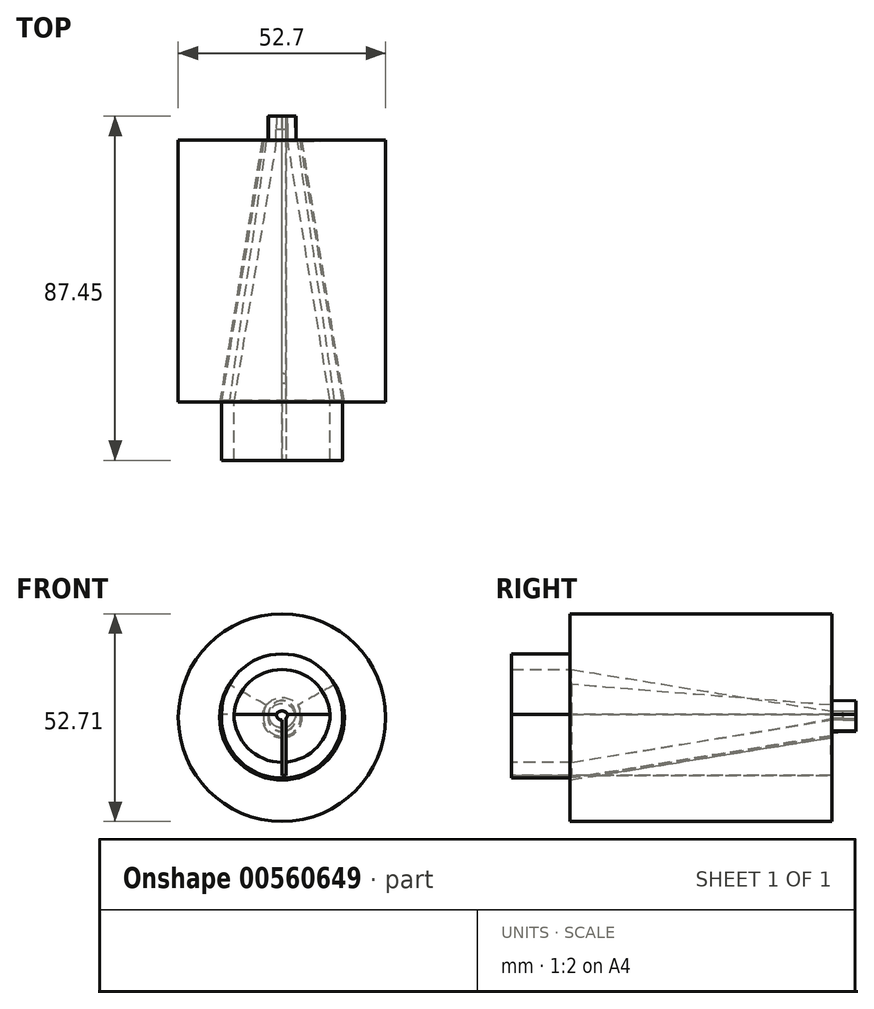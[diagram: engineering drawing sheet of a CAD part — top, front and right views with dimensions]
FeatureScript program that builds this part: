
annotation { "Feature Type Name" : "Feature", "Feature Type Description" : "" }
export const myFeature = defineFeature(function(context is Context, id is Id, definition is map)
    precondition{}
    {
        {
            var Q0;
            Q0=qCreatedBy(makeId("Top.planeOp"),FACE);
            var sketch = newSketch(context, id + "F0", { "sketchPlane" : qUnion([Q0])});
            skLineSegment(sketch, "E0", {"start": v(0, 62.44) * mm, "end": v(0, 0) * mm});
            skLineSegment(sketch, "E1", {"start": v(0, 0) * mm, "end": v(0, 87.31) * mm});
            skLineSegment(sketch, "E2", {"start": v(15.36, 0) * mm, "end": v(4.65, 65.87) * mm});
            skLineSegment(sketch, "E3", {"start": v(1.88, 63.36) * mm, "end": v(1.47, 65.87) * mm});
            skLineSegment(sketch, "E4", {"start": v(1.88, 63.36) * mm, "end": v(12.19, 0) * mm});
            skLineSegment(sketch, "E5", {"start": v(0, 0) * mm, "end": v(0, -15.24) * mm});
            skLineSegment(sketch, "E6", {"start": v(12.19, -15.24) * mm, "end": v(12.19, 0) * mm});
            skLineSegment(sketch, "E7", {"start": v(15.36, -15.24) * mm, "end": v(12.19, -15.24) * mm});
            skLineSegment(sketch, "E8", {"start": v(15.36, 0) * mm, "end": v(15.36, -15.24) * mm});
            skLineSegment(sketch, "E9", {"start": v(1.47, 65.87) * mm, "end": v(1.47, 68.94) * mm});
            skLineSegment(sketch, "E10", {"start": v(1.47, 68.94) * mm, "end": v(1.43, 72.19) * mm});
            skLineSegment(sketch, "E11", {"start": v(1.43, 72.19) * mm, "end": v(3.42, 72.21) * mm});
            skLineSegment(sketch, "E12", {"start": v(3.42, 72.21) * mm, "end": v(3.5, 65.87) * mm});
            skLineSegment(sketch, "E13", {"start": v(3.5, 65.87) * mm, "end": v(4.65, 65.87) * mm});
            skLineSegment(sketch, "E14", {"start": v(15.82, -0.39) * mm, "end": v(26.34, -0.39) * mm});
            skLineSegment(sketch, "E15", {"start": v(26.34, -0.39) * mm, "end": v(26.34, 65.1) * mm});
            skLineSegment(sketch, "E16", {"start": v(15.82, -0.39) * mm, "end": v(5.05, 65.87) * mm});
            skLineSegment(sketch, "E17", {"start": v(5.05, 65.87) * mm, "end": v(26.34, 66.14) * mm});
            skLineSegment(sketch, "E18", {"start": v(26.34, 66.14) * mm, "end": v(26.34, 65.1) * mm});
            skSolve(sketch);
        }
        {
            var Q0;
            Q0=makeQuery(id+"F0.imprint","IMPRINT",FACE,{"disambiguationData":[TD([[makeQuery(id+"F0.imprint","IMPRINT",EDGE,{"derivedFrom":sQuery(id+"F0.wireOp",EDGE,"9rF7vb6r-FRlw-Ho1k-BeVo-7rTsjgvCfUZn")}),-1.0]])]});
            var Q1;
            Q1=makeQuery(id+"F0.imprint","IMPRINT",FACE,{"disambiguationData":[TD([[makeQuery(id+"F0.imprint","IMPRINT",EDGE,{"derivedFrom":sQuery(id+"F0.wireOp",EDGE,"Z7jYxYJT-giHp-wwWC-82rW-opkupLNmgxhj")}),1.0]])]});
            var Q2;
            Q2=makeQuery(id+"F0.imprint","IMPRINT",FACE,{"disambiguationData":[TD([[makeQuery(id+"F0.imprint","IMPRINT",EDGE,{"derivedFrom":sQuery(id+"F0.wireOp",EDGE,"YAChQfTu-laHF-aghZ-eu0H-mjPeFCp4v3qm")}),1.0]])]});
            var Q3;
            Q3=makeQuery(id+"F0.imprint","IMPRINT",FACE,{"disambiguationData":[TD([[makeQuery(id+"F0.imprint","IMPRINT",EDGE,{"derivedFrom":sQuery(id+"F0.wireOp",EDGE,"7sCdhYLg-qufo-eqTT-VUgK-juI2TmZJkONH")}),1.0]])]});
            var Q4;
            Q4=makeQuery(id+"F0.imprint","IMPRINT",FACE,{"disambiguationData":[TD([[makeQuery(id+"F0.imprint","IMPRINT",EDGE,{"derivedFrom":sQuery(id+"F0.wireOp",EDGE,"lonxppou-iT4y-VWF7-XKBM-2UJHTexJlwN0")}),-1.0]])]});
            var Q5;
            Q5=makeQuery(id+"F0.imprint","IMPRINT",FACE,{"disambiguationData":[TD([[makeQuery(id+"F0.imprint","IMPRINT",EDGE,{"derivedFrom":sQuery(id+"F0.wireOp",EDGE,"E2")}),1.0]])]});
            var Q6;
            {var subQ0=sQuery(id+"F0.wireOp",EDGE,"E9");Q6=makeQuery(id+"F0.imprint","IMPRINT",FACE,{"disambiguationData":[TD([[makeQuery(id+"F0.imprint","IMPRINT",EDGE,{"derivedFrom":subQ0}),-1.0]])]});}
            var Q7;
            Q7=sQuery(id+"F0.wireOp",EDGE,"E1");
            revolve(context, id + "F1", {"entities" : qUnion([Q0, Q1, Q2, Q3, Q4, Q5, Q6]), "axis" : qUnion([Q7]), "revolveType" : RevolveType.FULL});
        }
        {
            var Q0;
            Q0=qCreatedBy(makeId("Right.planeOp"),FACE);
            var sketch = newSketch(context, id + "F2", { "sketchPlane" : qUnion([Q0])});
            skLineSegment(sketch, "E19", {"start": v(62.53, -0.82) * mm, "end": v(0, -0.82) * mm});
            skLineSegment(sketch, "E20", {"start": v(0, -0.82) * mm, "end": v(0, 1.73) * mm});
            skLineSegment(sketch, "E21", {"start": v(0, 1.73) * mm, "end": v(62.53, 1.73) * mm});
            skLineSegment(sketch, "E22", {"start": v(62.53, 1.73) * mm, "end": v(62.53, -0.82) * mm});
            skSolve(sketch);
        }
        {
            var Q0;
            Q0 = qSketchRegion(id + "F0", true);
            var Q1;
            Q1=sQuery(id+"F2.wireOp",EDGE,"E19");
            revolve(context, id + "F3", {"operationType" : NewBodyOperationType.ADD, "entities" : qUnion([Q0]), "axis" : qUnion([Q1]), "revolveType" : RevolveType.FULL});
        }
        {
            var Q0;
            Q0=qCreatedBy(makeId("Top.planeOp"),FACE);
            var sketch = newSketch(context, id + "F4", { "sketchPlane" : qUnion([Q0])});
            skLineSegment(sketch, "E23", {"start": v(0, -173.25) * mm, "end": v(0, 818.48) * mm});
            skLineSegment(sketch, "E24", {"start": v(0, 818.48) * mm, "end": v(1, 818.48) * mm});
            skLineSegment(sketch, "E25", {"start": v(1, 818.48) * mm, "end": v(1, -173.25) * mm});
            skLineSegment(sketch, "E26", {"start": v(1, -173.25) * mm, "end": v(0, -173.25) * mm});
            skSolve(sketch);
        }
        {
            var Q0;
            Q0 = qSketchRegion(id + "F4", true);
            extrude(context, id + "F5", {"entities" : qUnion([Q0]), "operationType" : NewBodyOperationType.REMOVE, "oppositeDirection" : true, "depth" : 15.5 * mm, "offsetDistance" : 25 * mm});
        }
    });
